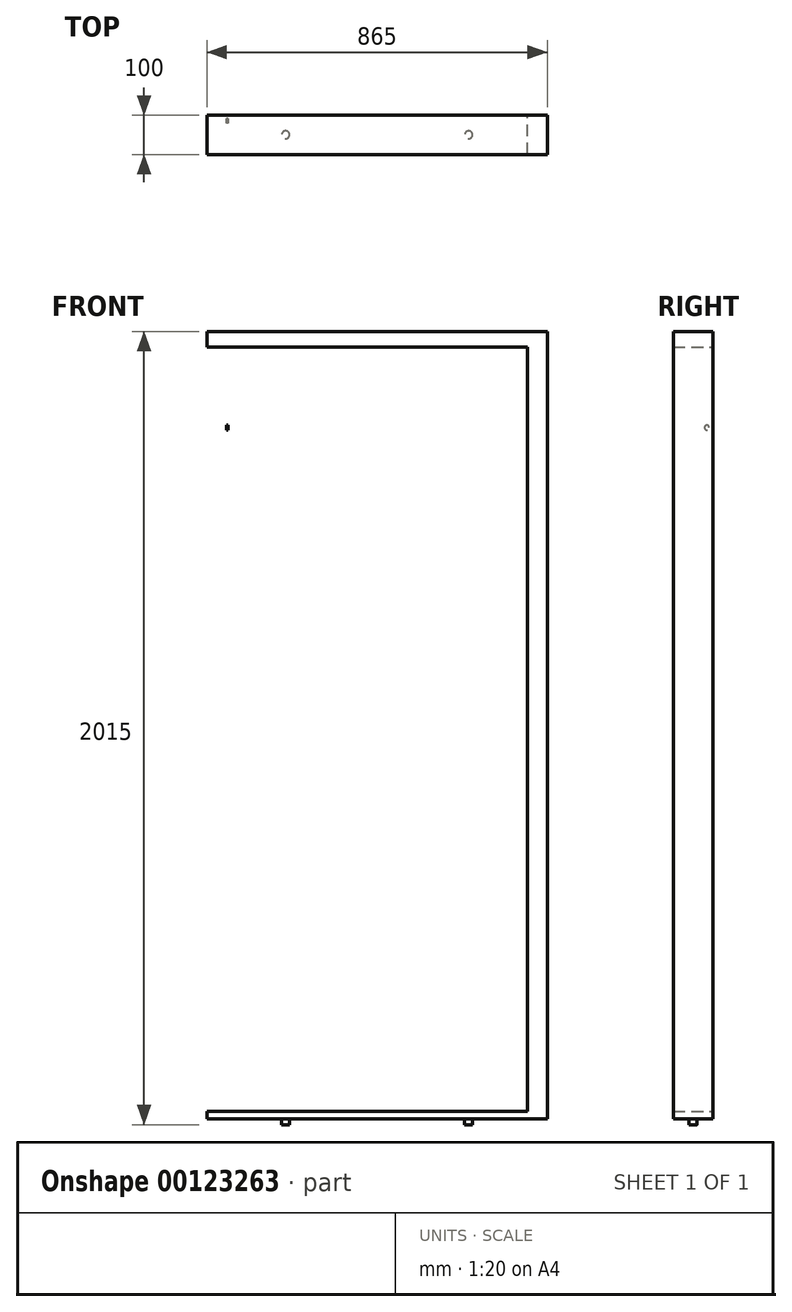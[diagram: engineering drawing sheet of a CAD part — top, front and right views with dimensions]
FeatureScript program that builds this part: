
annotation { "Feature Type Name" : "Feature", "Feature Type Description" : "" }
export const myFeature = defineFeature(function(context is Context, id is Id, definition is map)
    precondition{}
    {
        {
            var Q0;
            Q0=qCreatedBy(makeId("Front.planeOp"),FACE);
            var sketch = newSketch(context, id + "F0", { "sketchPlane" : qUnion([Q0])});
            skLineSegment(sketch, "E0.bottom", {"start": v(-432.5, 990) * mm, "end": v(432.5, 990) * mm});
            skLineSegment(sketch, "E0.top", {"start": v(-432.5, 971) * mm, "end": v(432.5, 971) * mm});
            skLineSegment(sketch, "E0.left", {"start": v(-432.5, 990) * mm, "end": v(-432.5, 971) * mm});
            skLineSegment(sketch, "E0.right", {"start": v(432.5, 990) * mm, "end": v(432.5, 971) * mm});
            skLineSegment(sketch, "E1.top", {"start": v(-432.5, 1010) * mm, "end": v(432.5, 1010) * mm});
            skLineSegment(sketch, "E1.left", {"start": v(-432.5, 990) * mm, "end": v(-432.5, 1010) * mm});
            skLineSegment(sketch, "E1.right", {"start": v(432.5, 990) * mm, "end": v(432.5, 1010) * mm});
            skLineSegment(sketch, "E2.bottom", {"start": v(-432.5, 971) * mm, "end": v(-382.5, 971) * mm});
            skLineSegment(sketch, "E2.top", {"start": v(-432.5, -971) * mm, "end": v(-382.5, -971) * mm});
            skLineSegment(sketch, "E2.left", {"start": v(-432.5, 971) * mm, "end": v(-432.5, -971) * mm});
            skLineSegment(sketch, "E2.right", {"start": v(-382.5, 971) * mm, "end": v(-382.5, -971) * mm});
            skLineSegment(sketch, "E3.MirrorCS", {"start": v(432.5, 971) * mm, "end": v(432.5, -971) * mm});
            skLineSegment(sketch, "E4.MirrorCS", {"start": v(382.5, 971) * mm, "end": v(382.5, -971) * mm});
            skLineSegment(sketch, "E5.MirrorCS", {"start": v(432.5, -971) * mm, "end": v(382.5, -971) * mm});
            skLineSegment(sketch, "E6.MirrorCS", {"start": v(432.5, 971) * mm, "end": v(382.5, 971) * mm});
            skLineSegment(sketch, "E7.MirrorCS", {"start": v(-432.5, -990) * mm, "end": v(432.5, -990) * mm});
            skLineSegment(sketch, "E8.MirrorCS", {"start": v(-432.5, -971) * mm, "end": v(432.5, -971) * mm});
            skLineSegment(sketch, "E9.MirrorCS", {"start": v(-432.5, -990) * mm, "end": v(-432.5, -971) * mm});
            skLineSegment(sketch, "E10.MirrorCS", {"start": v(432.5, -990) * mm, "end": v(432.5, -971) * mm});
            skSolve(sketch);
        }
        {
            var Q0;
            Q0=makeQuery(id+"F0.imprint","IMPRINT",FACE,{"disambiguationData":[TD([[makeQuery(id+"F0.imprint","IMPRINT",EDGE,{"derivedFrom":sQuery(id+"F0.wireOp",EDGE,"E2.bottom")}),-1.0]])]});
            var Q1;
            Q1=makeQuery(id+"F0.imprint","IMPRINT",FACE,{"disambiguationData":[TD([[makeQuery(id+"F0.imprint","IMPRINT",EDGE,{"derivedFrom":sQuery(id+"F0.wireOp",EDGE,"E0.top")}),1.0]])]});
            var Q2;
            Q2=makeQuery(id+"F0.imprint","IMPRINT",FACE,{"disambiguationData":[TD([[makeQuery(id+"F0.imprint","IMPRINT",EDGE,{"derivedFrom":sQuery(id+"F0.wireOp",EDGE,"E0.bottom")}),1.0]])]});
            var Q3;
            {var subQ0=sQuery(id+"F0.wireOp",EDGE,"E3.MirrorCS");Q3=makeQuery(id+"F0.imprint","IMPRINT",FACE,{"disambiguationData":[TD([[makeQuery(id+"F0.imprint","IMPRINT",EDGE,{"derivedFrom":subQ0}),-1.0]])]});}
            var Q4;
            Q4=makeQuery(id+"F0.imprint","IMPRINT",FACE,{"disambiguationData":[TD([[makeQuery(id+"F0.imprint","IMPRINT",EDGE,{"derivedFrom":sQuery(id+"F0.wireOp",EDGE,"E7.MirrorCS")}),1.0]])]});
            extrude(context, id + "F1", {"entities" : qUnion([Q0, Q1, Q2, Q3, Q4]), "endBound" : BoundingType.SYMMETRIC, "depth" : 100 * mm});
        }
        {
            var Q0;
            Q0=qCreatedBy(makeId("Top.planeOp"),FACE);
            cPlane(context, id + "F2", {"entities" : qUnion([Q0]), "cplaneType" : CPlaneType.OFFSET, "offset" : 990 * mm, "oppositeDirection" : true, "width" : 150 * mm, "height" : 150 * mm});
        }
        {
            var Q0;
            Q0=qCreatedBy(id+"F2.planeOp",FACE);
            var sketch = newSketch(context, id + "F3", { "sketchPlane" : qUnion([Q0])});
            skCircle(sketch, "E11", {"center": v(-232.5, 0) * mm, "radius": 10 * mm});
            skCircle(sketch, "E12.MirrorC", {"center": v(232.5, 0) * mm, "radius": 10 * mm});
            skSolve(sketch);
        }
        {
            var Q0;
            Q0 = qSketchRegion(id + "F3", true);
            extrude(context, id + "F4", {"entities" : qUnion([Q0]), "operationType" : NewBodyOperationType.ADD, "oppositeDirection" : true, "depth" : 15 * mm});
        }
        {
            var Q0;
            Q0=qCreatedBy(makeId("Right.planeOp"),FACE);
            cPlane(context, id + "F5", {"entities" : qUnion([Q0]), "cplaneType" : CPlaneType.OFFSET, "offset" : 382.5 * mm, "oppositeDirection" : true, "width" : 150 * mm, "height" : 150 * mm});
        }
        {
            var Q0;
            Q0=qCreatedBy(id+"F5.planeOp",FACE);
            var sketch = newSketch(context, id + "F6", { "sketchPlane" : qUnion([Q0])});
            skCircle(sketch, "E13", {"center": v(35, 766) * mm, "radius": 6 * mm});
            skCircle(sketch, "E14.MirrorC", {"center": v(35, -766) * mm, "radius": 6 * mm});
            skSolve(sketch);
        }
        {
            var Q0;
            Q0=makeQuery(id+"F6.imprint","IMPRINT",FACE,{"disambiguationData":[TD([[makeQuery(id+"F6.imprint","IMPRINT",EDGE,{"derivedFrom":sQuery(id+"F6.wireOp",EDGE,"E13")}),1.0]])]});
            var Q1;
            Q1=makeQuery(id+"F6.imprint","IMPRINT",FACE,{"disambiguationData":[TD([[makeQuery(id+"F6.imprint","IMPRINT",EDGE,{"derivedFrom":sQuery(id+"F6.wireOp",EDGE,"E14.MirrorC")}),-1.0]])]});
            extrude(context, id + "F7", {"entities" : qUnion([Q0, Q1]), "operationType" : NewBodyOperationType.ADD, "depth" : 4 * mm});
        }
    });
